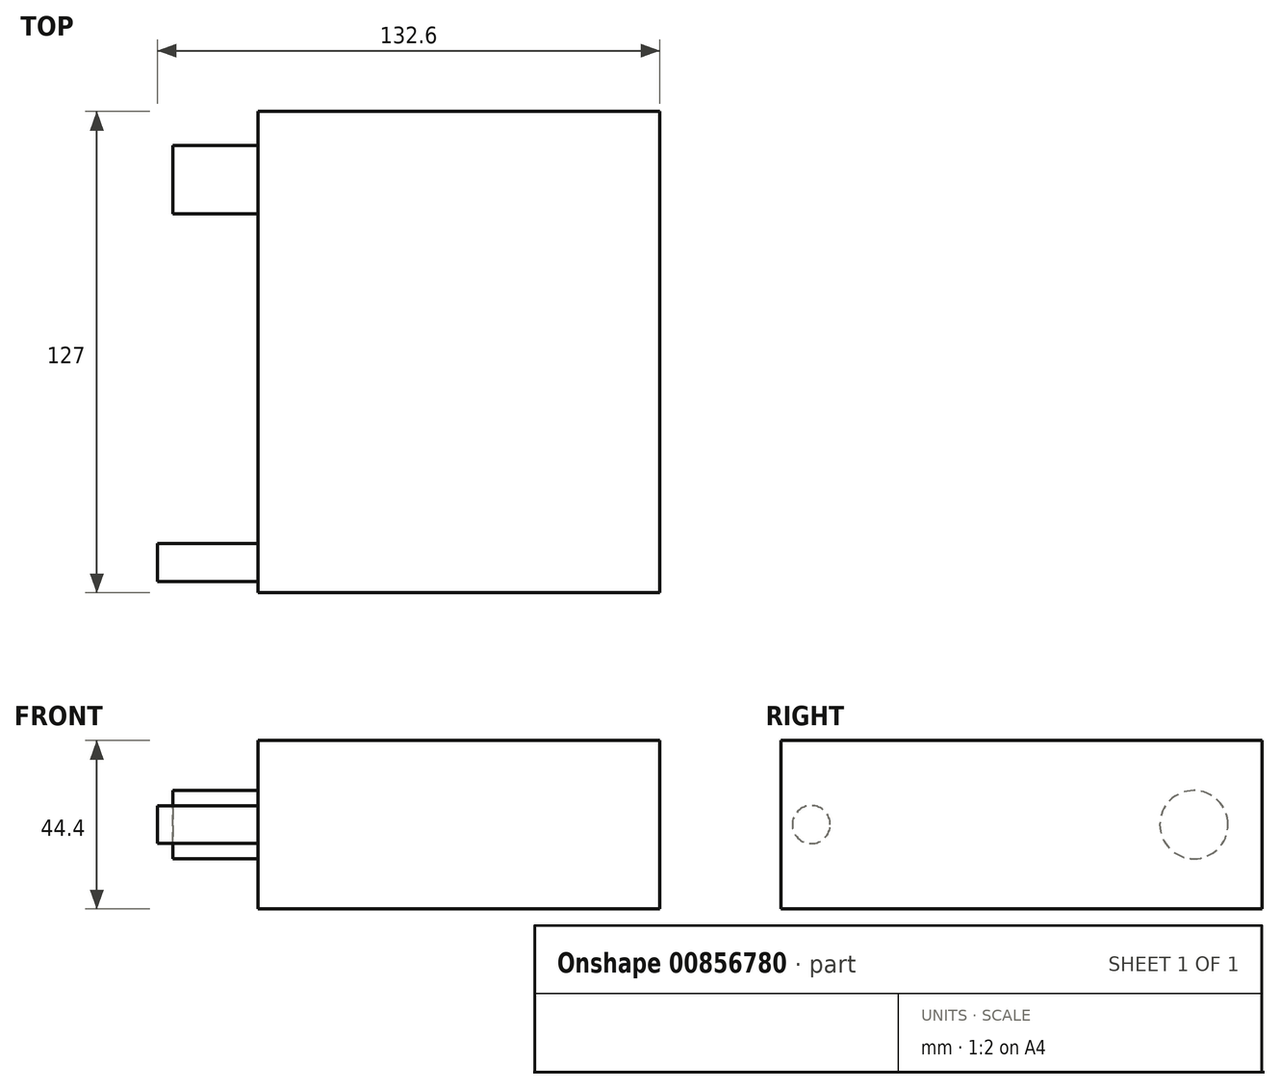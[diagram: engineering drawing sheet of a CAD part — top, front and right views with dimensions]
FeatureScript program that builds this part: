
annotation { "Feature Type Name" : "Feature", "Feature Type Description" : "" }
export const myFeature = defineFeature(function(context is Context, id is Id, definition is map)
    precondition{}
    {
        {
            var Q0;
            Q0=qCreatedBy(makeId("Top.planeOp"),FACE);
            var sketch = newSketch(context, id + "F0", { "sketchPlane" : qUnion([Q0])});
            skLineSegment(sketch, "E0.bottom", {"start": v(0, 0) * mm, "end": v(-106, 0) * mm});
            skLineSegment(sketch, "E0.top", {"start": v(0, 127) * mm, "end": v(-106, 127) * mm});
            skLineSegment(sketch, "E0.left", {"start": v(0, 0) * mm, "end": v(0, 127) * mm});
            skLineSegment(sketch, "E0.right", {"start": v(-106, 0) * mm, "end": v(-106, 127) * mm});
            skSolve(sketch);
        }
        {
            var Q0;
            Q0=makeQuery(id+"F0.imprint","IMPRINT",FACE,{"disambiguationData":[TD([[makeQuery(id+"F0.imprint","IMPRINT",EDGE,{"derivedFrom":sQuery(id+"F0.wireOp",EDGE,"E0.bottom")}),-1.0]])]});
            extrude(context, id + "F1", {"entities" : qUnion([Q0]), "depth" : 44.4 * mm, "offsetDistance" : 25 * mm});
        }
        {
            var Q0;
            Q0=makeQuery(id+"F1.opExtrude","SWEPT_FACE",FACE,{"disambiguationData":[OSD([sQuery(id+"F0.wireOp",EDGE,"E0.right")])]});
            var sketch = newSketch(context, id + "F2", { "sketchPlane" : qUnion([Q0])});
            skCircle(sketch, "E1", {"center": v(-109, 22.2) * mm, "radius": 9 * mm});
            skPoint(sketch, "E1.centerSnap0", {"position": v(-127, 22.2) * mm});
            skCircle(sketch, "E2", {"center": v(-8, 22.2) * mm, "radius": 5 * mm});
            skSolve(sketch);
        }
        {
            var Q0;
            Q0=makeQuery(id+"F2.imprint","IMPRINT",FACE,{"disambiguationData":[TD([[makeQuery(id+"F2.imprint","IMPRINT",EDGE,{"derivedFrom":sQuery(id+"F2.wireOp",EDGE,"E1")}),1.0]])]});
            extrude(context, id + "F3", {"entities" : qUnion([Q0]), "operationType" : NewBodyOperationType.ADD, "depth" : 22.5 * mm, "offsetDistance" : 25 * mm});
        }
        {
            var Q0;
            Q0=makeQuery(id+"F2.imprint","IMPRINT",FACE,{"disambiguationData":[TD([[makeQuery(id+"F2.imprint","IMPRINT",EDGE,{"derivedFrom":sQuery(id+"F2.wireOp",EDGE,"E2")}),1.0]])]});
            extrude(context, id + "F4", {"entities" : qUnion([Q0]), "operationType" : NewBodyOperationType.ADD, "depth" : 26.6 * mm, "offsetDistance" : 25 * mm});
        }
    });
